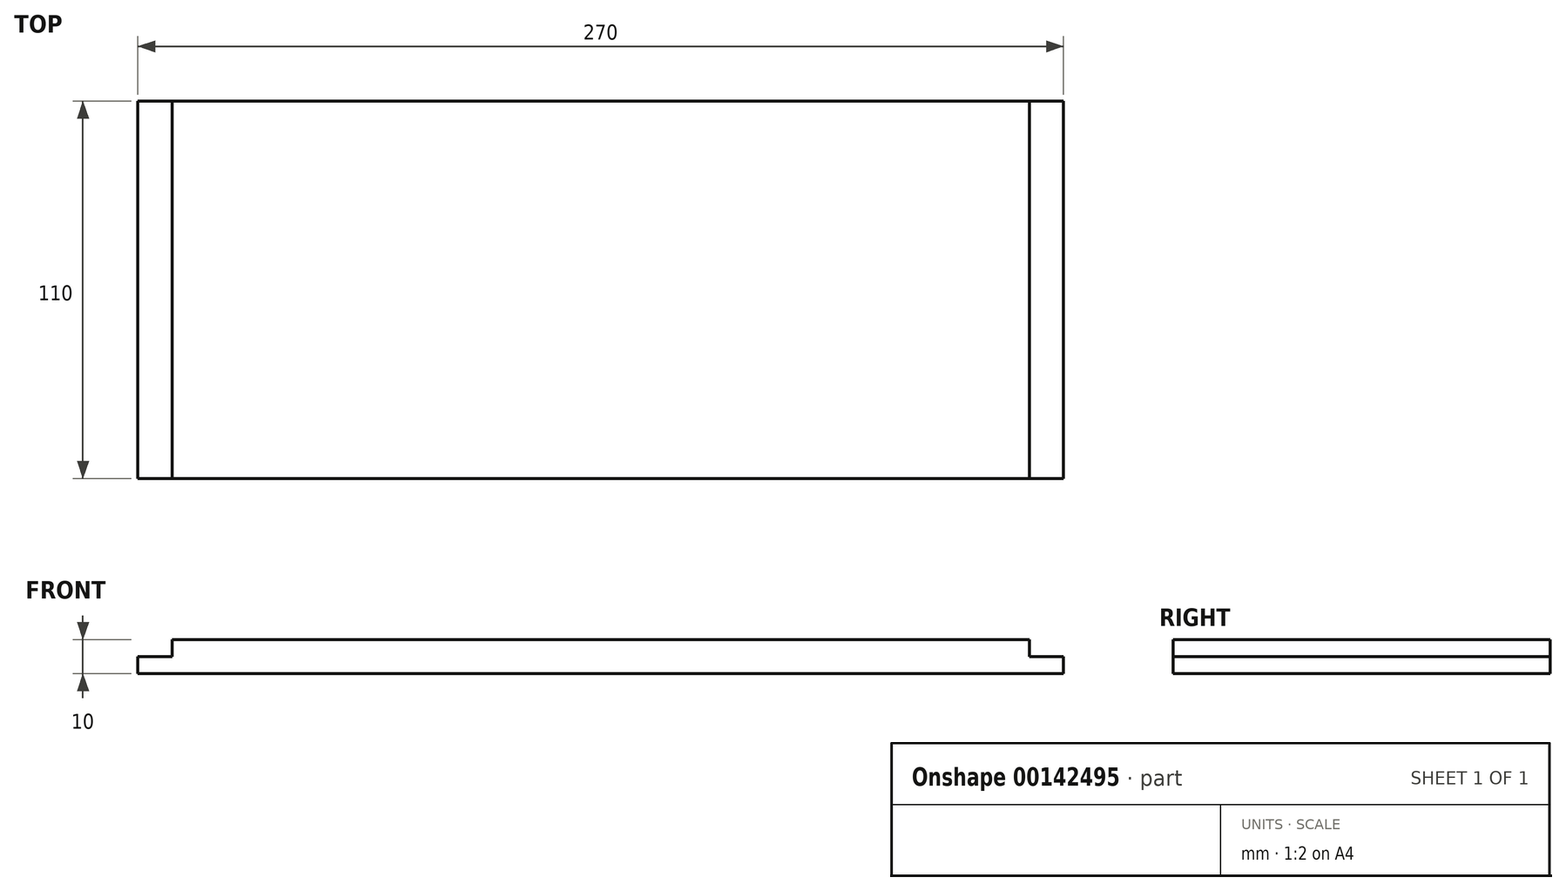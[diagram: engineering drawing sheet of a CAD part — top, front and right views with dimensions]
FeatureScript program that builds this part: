
annotation { "Feature Type Name" : "Feature", "Feature Type Description" : "" }
export const myFeature = defineFeature(function(context is Context, id is Id, definition is map)
    precondition{}
    {
        {
            var Q0;
            Q0=qCreatedBy(makeId("Top.planeOp"),FACE);
            var sketch = newSketch(context, id + "F0", { "sketchPlane" : qUnion([Q0])});
            skLineSegment(sketch, "E0.bottom", {"start": v(-135, 63.88) * mm, "end": v(135, 63.88) * mm});
            skLineSegment(sketch, "E0.top", {"start": v(-135, -46.12) * mm, "end": v(135, -46.12) * mm});
            skLineSegment(sketch, "E0.left", {"start": v(-135, 63.88) * mm, "end": v(-135, -46.12) * mm});
            skLineSegment(sketch, "E0.right", {"start": v(135, 63.88) * mm, "end": v(135, -46.12) * mm});
            skSolve(sketch);
        }
        {
            var Q0;
            Q0=makeQuery(id+"F0.imprint","IMPRINT",FACE,{"disambiguationData":[TD([[makeQuery(id+"F0.imprint","IMPRINT",EDGE,{"derivedFrom":sQuery(id+"F0.wireOp",EDGE,"E0.bottom")}),-1.0]])]});
            extrude(context, id + "F1", {"entities" : qUnion([Q0]), "depth" : 10 * mm});
        }
        {
            var Q0;
            Q0=makeQuery(id+"F1.opExtrude","CAP_FACE",FACE,{"disambiguationData":[OSD([sQuery(id+"F0.wireOp",EDGE,"E0.bottom"),sQuery(id+"F0.wireOp",EDGE,"E0.top"),sQuery(id+"F0.wireOp",EDGE,"E0.left"),sQuery(id+"F0.wireOp",EDGE,"E0.right")])],"isStart":false});
            var sketch = newSketch(context, id + "F2", { "sketchPlane" : qUnion([Q0])});
            skLineSegment(sketch, "E1.bottom", {"start": v(-135, 63.88) * mm, "end": v(-125, 63.88) * mm});
            skLineSegment(sketch, "E1.top", {"start": v(-135, -46.12) * mm, "end": v(-125, -46.12) * mm});
            skLineSegment(sketch, "E1.left", {"start": v(-135, 63.88) * mm, "end": v(-135, -46.12) * mm});
            skLineSegment(sketch, "E1.right", {"start": v(-125, 63.88) * mm, "end": v(-125, -46.12) * mm});
            skLineSegment(sketch, "E2.MirrorCS", {"start": v(135, 63.88) * mm, "end": v(125, 63.88) * mm});
            skLineSegment(sketch, "E3.MirrorCS", {"start": v(135, 63.88) * mm, "end": v(135, -46.12) * mm});
            skLineSegment(sketch, "E4.MirrorCS", {"start": v(135, -46.12) * mm, "end": v(125, -46.12) * mm});
            skLineSegment(sketch, "E5.MirrorCS", {"start": v(125, 63.88) * mm, "end": v(125, -46.12) * mm});
            skSolve(sketch);
        }
        {
            var Q0;
            Q0 = qSketchRegion(id + "F2", true);
            extrude(context, id + "F3", {"entities" : qUnion([Q0]), "operationType" : NewBodyOperationType.REMOVE, "oppositeDirection" : true, "depth" : 5 * mm});
        }
    });
